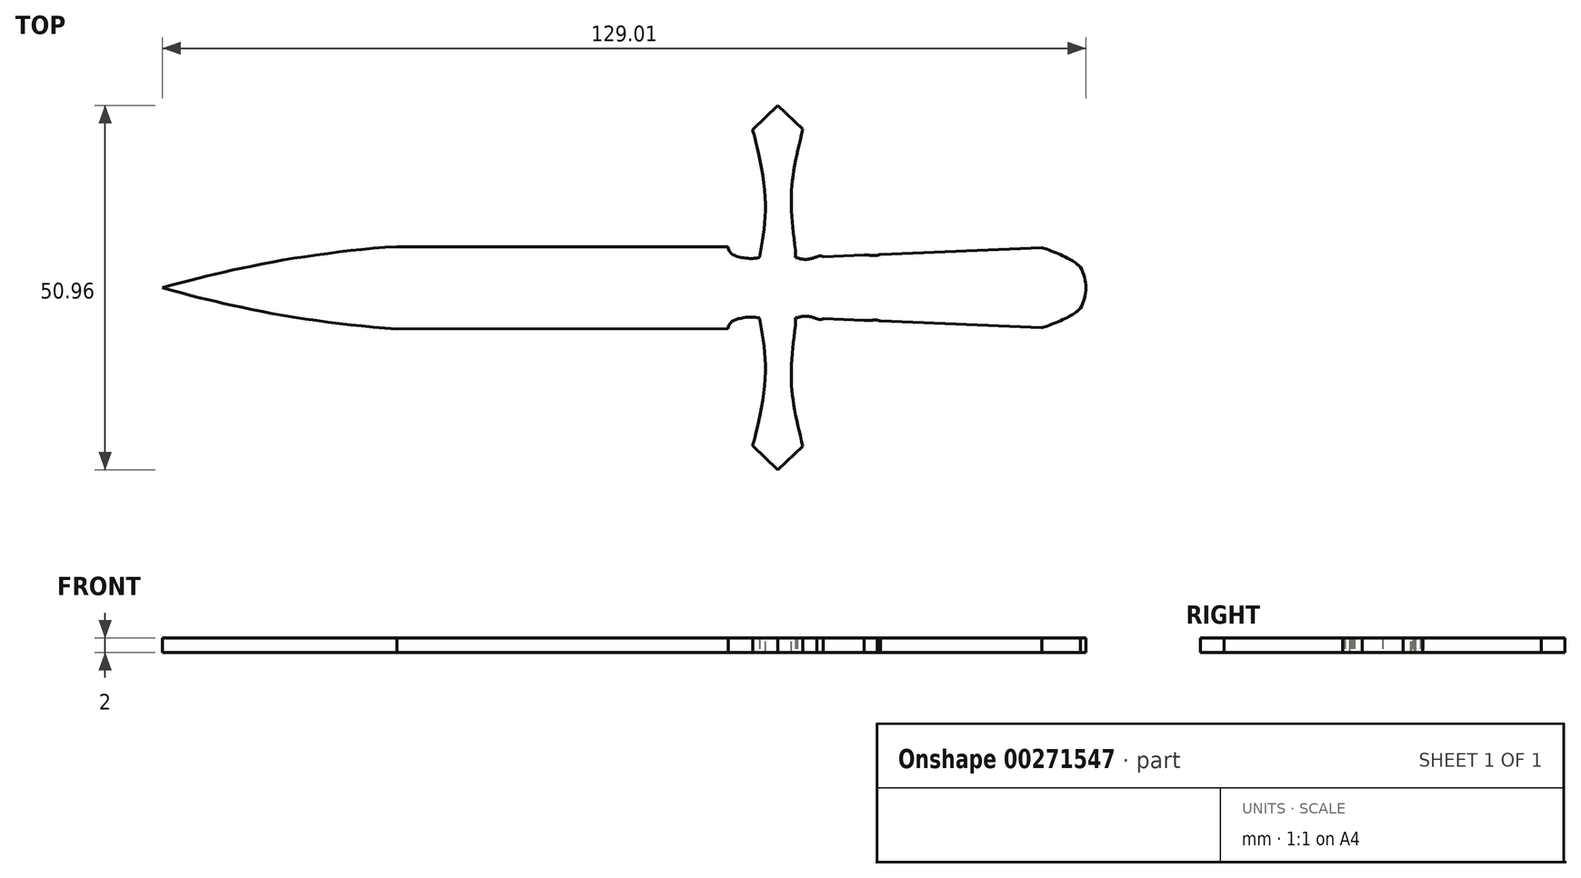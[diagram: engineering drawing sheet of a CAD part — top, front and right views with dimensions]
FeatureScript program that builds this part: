
annotation { "Feature Type Name" : "Feature", "Feature Type Description" : "" }
export const myFeature = defineFeature(function(context is Context, id is Id, definition is map)
    precondition{}
    {
        {
            var Q0;
            Q0=qCreatedBy(makeId("Top.planeOp"),FACE);
            var sketch = newSketch(context, id + "F0", { "sketchPlane" : qUnion([Q0])});
            skLineSegment(sketch, "E0", {"start": v(8.9, 6.17) * mm, "end": v(-19.47, 6.17) * mm});
            skFitSpline(sketch, "E1", {"points": [v(8.9, 6.17) * mm, v(8.67, 5.7) * mm, v(9, 4.88) * mm, v(10.35, 4.27) * mm, v(12.08, 4.1) * mm, v(13.02, 4.24) * mm], "startDerivative": vector(-2.22, -3.07) * mm, "endDerivative": vector(4.57, 1.03) * mm});
            skFitSpline(sketch, "E2", {"points": [v(13.02, 4.24) * mm, v(13.8, 12.78) * mm, v(12.23, 21.56) * mm, v(12.06, 22.1) * mm], "startDerivative": vector(3.45, 17.75) * mm, "endDerivative": vector(-1.16, 3.1) * mm});
            skLineSegment(sketch, "E3", {"start": v(12.06, 22.1) * mm, "end": v(15.59, 25.48) * mm});
            skLineSegment(sketch, "E4", {"start": v(15.59, 25.48) * mm, "end": v(19.08, 22.16) * mm});
            skLineSegment(sketch, "E5", {"start": v(18.05, 5.27) * mm, "end": v(18.05, 4.2) * mm});
            skLineSegment(sketch, "E6", {"start": v(18.05, 4.2) * mm, "end": v(18.28, 4.2) * mm});
            skFitSpline(sketch, "E7", {"points": [v(18.28, 4.2) * mm, v(19.45, 3.96) * mm, v(21.06, 4.33) * mm], "startDerivative": vector(2.44, -0.79) * mm, "endDerivative": vector(3.1, 1) * mm});
            skFitSpline(sketch, "E8", {"points": [v(21.06, 4.33) * mm, v(21.52, 4.46) * mm, v(21.94, 4.33) * mm], "startDerivative": vector(0.92, 0.39) * mm, "endDerivative": vector(0.84, -0.4) * mm});
            skFitSpline(sketch, "E9", {"points": [v(-19.47, 6.17) * mm, v(-27.9, 5.95) * mm, v(-37.61, 5.75) * mm, v(-46.1, 4.95) * mm, v(-54.03, 3.78) * mm, v(-60.49, 2.48) * mm, v(-65.08, 1.43) * mm, v(-70.4, 0) * mm], "startDerivative": vector(-53.4, -1.72) * mm, "endDerivative": vector(-43.93, -12.14) * mm});
            skFitSpline(sketch, "E10.MirrorCS", {"points": [v(-19.47, -6.17) * mm, v(-27.9, -5.95) * mm, v(-37.61, -5.75) * mm, v(-46.1, -4.95) * mm, v(-54.03, -3.78) * mm, v(-60.49, -2.48) * mm, v(-65.08, -1.43) * mm, v(-70.4, 0) * mm], "startDerivative": vector(-53.4, 1.72) * mm, "endDerivative": vector(-43.93, 12.14) * mm});
            skLineSegment(sketch, "E11.MirrorCS", {"start": v(8.9, -6.17) * mm, "end": v(-19.47, -6.17) * mm});
            skFitSpline(sketch, "E12.MirrorCS", {"points": [v(8.9, -6.17) * mm, v(8.67, -5.7) * mm, v(9, -4.88) * mm, v(10.35, -4.27) * mm, v(12.08, -4.1) * mm, v(13.02, -4.24) * mm], "startDerivative": vector(-2.22, 3.07) * mm, "endDerivative": vector(4.57, -1.03) * mm});
            skFitSpline(sketch, "E13.MirrorCS", {"points": [v(13.02, -4.24) * mm, v(13.8, -12.78) * mm, v(12.23, -21.56) * mm, v(12.06, -22.1) * mm], "startDerivative": vector(3.45, -17.75) * mm, "endDerivative": vector(-1.16, -3.1) * mm});
            skLineSegment(sketch, "E14.MirrorCS", {"start": v(12.06, -22.1) * mm, "end": v(15.59, -25.48) * mm});
            skLineSegment(sketch, "E15.MirrorCS", {"start": v(15.59, -25.48) * mm, "end": v(19.08, -22.16) * mm});
            skLineSegment(sketch, "E16.MirrorCS", {"start": v(18.05, -5.27) * mm, "end": v(18.05, -4.2) * mm});
            skLineSegment(sketch, "E17.MirrorCS", {"start": v(18.05, -4.2) * mm, "end": v(18.28, -4.2) * mm});
            skFitSpline(sketch, "E18.MirrorCS", {"points": [v(18.28, -4.2) * mm, v(19.45, -3.96) * mm, v(21.06, -4.33) * mm], "startDerivative": vector(2.44, 0.79) * mm, "endDerivative": vector(3.1, -1) * mm});
            skFitSpline(sketch, "E19.MirrorCS", {"points": [v(21.06, -4.33) * mm, v(21.52, -4.46) * mm, v(21.94, -4.33) * mm], "startDerivative": vector(0.92, -0.39) * mm, "endDerivative": vector(0.84, 0.4) * mm});
            skFitSpline(sketch, "E20", {"points": [v(21.94, 4.33) * mm, v(26.13, 4.56) * mm, v(29.46, 4.51) * mm], "startDerivative": vector(8.15, 0.58) * mm, "endDerivative": vector(6.87, -0.21) * mm});
            skFitSpline(sketch, "E21", {"points": [v(29.46, 4.51) * mm, v(30.7, 4.82) * mm, v(33.74, 5.01) * mm, v(34.68, 4.97) * mm], "startDerivative": vector(3.44, 1.14) * mm, "endDerivative": vector(2.97, -0.25) * mm});
            skFitSpline(sketch, "E22", {"points": [v(34.68, 4.97) * mm, v(35.68, 5.21) * mm, v(43.1, 5.65) * mm, v(46.04, 5.42) * mm], "startDerivative": vector(3.67, 1.3) * mm, "endDerivative": vector(7.37, -1.05) * mm});
            skFitSpline(sketch, "E23", {"points": [v(46.04, 5.42) * mm, v(47.36, 5.82) * mm, v(51.44, 5.78) * mm, v(51.83, 5.59) * mm], "startDerivative": vector(3.18, 1.54) * mm, "endDerivative": vector(1.37, -1.24) * mm});
            skFitSpline(sketch, "E24", {"points": [v(51.83, 5.59) * mm, v(52.49, 5.59) * mm, v(56.69, 3.79) * mm, v(57.86, 2.86) * mm], "startDerivative": vector(2.42, 0.56) * mm, "endDerivative": vector(2.78, -2.81) * mm});
            skFitSpline(sketch, "E25", {"points": [v(57.86, 2.86) * mm, v(58.7, 2.15) * mm, v(59.9, 1.94) * mm, v(60.5, 2.04) * mm], "startDerivative": vector(2.03, -2.3) * mm, "endDerivative": vector(2, 0.49) * mm});
            skLineSegment(sketch, "E26", {"start": v(60.5, 2.04) * mm, "end": v(60.5, 3.9) * mm});
            skLineSegment(sketch, "E27", {"start": v(60.5, 3.9) * mm, "end": v(62.27, 4.79) * mm});
            skFitSpline(sketch, "E28", {"points": [v(62.27, 4.79) * mm, v(66.43, 3.67) * mm, v(69.82, 1.3) * mm, v(71.1, 0) * mm], "startDerivative": vector(11.13, -1.92) * mm, "endDerivative": vector(4.42, -4.83) * mm});
            skFitSpline(sketch, "E29.MirrorCS", {"points": [v(62.27, -4.79) * mm, v(66.43, -3.67) * mm, v(69.82, -1.3) * mm, v(71.1, 0) * mm], "startDerivative": vector(11.13, 1.92) * mm, "endDerivative": vector(4.42, 4.83) * mm});
            skLineSegment(sketch, "E30.MirrorCS", {"start": v(60.5, -3.9) * mm, "end": v(62.27, -4.79) * mm});
            skLineSegment(sketch, "E31.MirrorCS", {"start": v(60.5, -2.04) * mm, "end": v(60.5, -3.9) * mm});
            skFitSpline(sketch, "E32.MirrorCS", {"points": [v(57.86, -2.86) * mm, v(58.7, -2.15) * mm, v(59.9, -1.94) * mm, v(60.5, -2.04) * mm], "startDerivative": vector(2.03, 2.3) * mm, "endDerivative": vector(2, -0.49) * mm});
            skFitSpline(sketch, "E33.MirrorCS", {"points": [v(51.83, -5.59) * mm, v(52.49, -5.59) * mm, v(56.69, -3.79) * mm, v(57.86, -2.86) * mm], "startDerivative": vector(2.42, -0.56) * mm, "endDerivative": vector(2.78, 2.81) * mm});
            skFitSpline(sketch, "E34.MirrorCS", {"points": [v(46.04, -5.42) * mm, v(47.36, -5.82) * mm, v(51.44, -5.78) * mm, v(51.83, -5.59) * mm], "startDerivative": vector(3.18, -1.54) * mm, "endDerivative": vector(1.37, 1.24) * mm});
            skFitSpline(sketch, "E35.MirrorCS", {"points": [v(34.68, -4.97) * mm, v(35.68, -5.21) * mm, v(43.1, -5.65) * mm, v(46.04, -5.42) * mm], "startDerivative": vector(3.67, -1.3) * mm, "endDerivative": vector(7.37, 1.05) * mm});
            skFitSpline(sketch, "E36.MirrorCS", {"points": [v(29.46, -4.51) * mm, v(30.7, -4.82) * mm, v(33.74, -5.01) * mm, v(34.68, -4.97) * mm], "startDerivative": vector(3.44, -1.14) * mm, "endDerivative": vector(2.97, 0.25) * mm});
            skFitSpline(sketch, "E37.MirrorCS", {"points": [v(21.94, -4.33) * mm, v(26.13, -4.56) * mm, v(29.46, -4.51) * mm], "startDerivative": vector(8.15, -0.58) * mm, "endDerivative": vector(6.87, 0.21) * mm});
            skFitSpline(sketch, "E38", {"points": [v(19.08, 22.16) * mm, v(17.87, 16.64) * mm, v(17.46, 11.55) * mm, v(18.05, 5.27) * mm], "startDerivative": vector(-4.1, -16.85) * mm, "endDerivative": vector(2.31, -18.4) * mm});
            skFitSpline(sketch, "E39.MirrorCS", {"points": [v(19.08, -22.16) * mm, v(17.87, -16.64) * mm, v(17.46, -11.55) * mm, v(18.05, -5.27) * mm], "startDerivative": vector(-4.1, 16.85) * mm, "endDerivative": vector(2.31, 18.4) * mm});
            skLineSegment(sketch, "E40", {"start": v(52.49, 5.59) * mm, "end": v(21.94, 4.33) * mm});
            skLineSegment(sketch, "E41", {"start": v(21.94, -4.33) * mm, "end": v(52.49, -5.59) * mm});
            skArc(sketch, "E42", {"start": v(57.86, -2.86) * mm, "mid": v(58.62, 0) * mm, "end": v(57.86, 2.86) * mm});
            skLineSegment(sketch, "E43", {"start": v(-37.61, -5.75) * mm, "end": v(8.67, -5.7) * mm});
            skLineSegment(sketch, "E44", {"start": v(-37.61, 5.75) * mm, "end": v(8.67, 5.7) * mm});
            skSolve(sketch);
        }
        {
            var Q0;
            {var subQ15=sQuery(id+"F0.wireOp",EDGE,"E2");Q0=makeQuery(id+"F0.imprint","IMPRINT",FACE,{"disambiguationData":[TD([[makeQuery(id+"F0.imprint","IMPRINT",EDGE,{"derivedFrom":subQ15}),-1.0]])]});}
            extrude(context, id + "F1", {"entities" : qUnion([Q0]), "depth" : 2 * mm, "offsetDistance" : 25 * mm});
        }
    });
